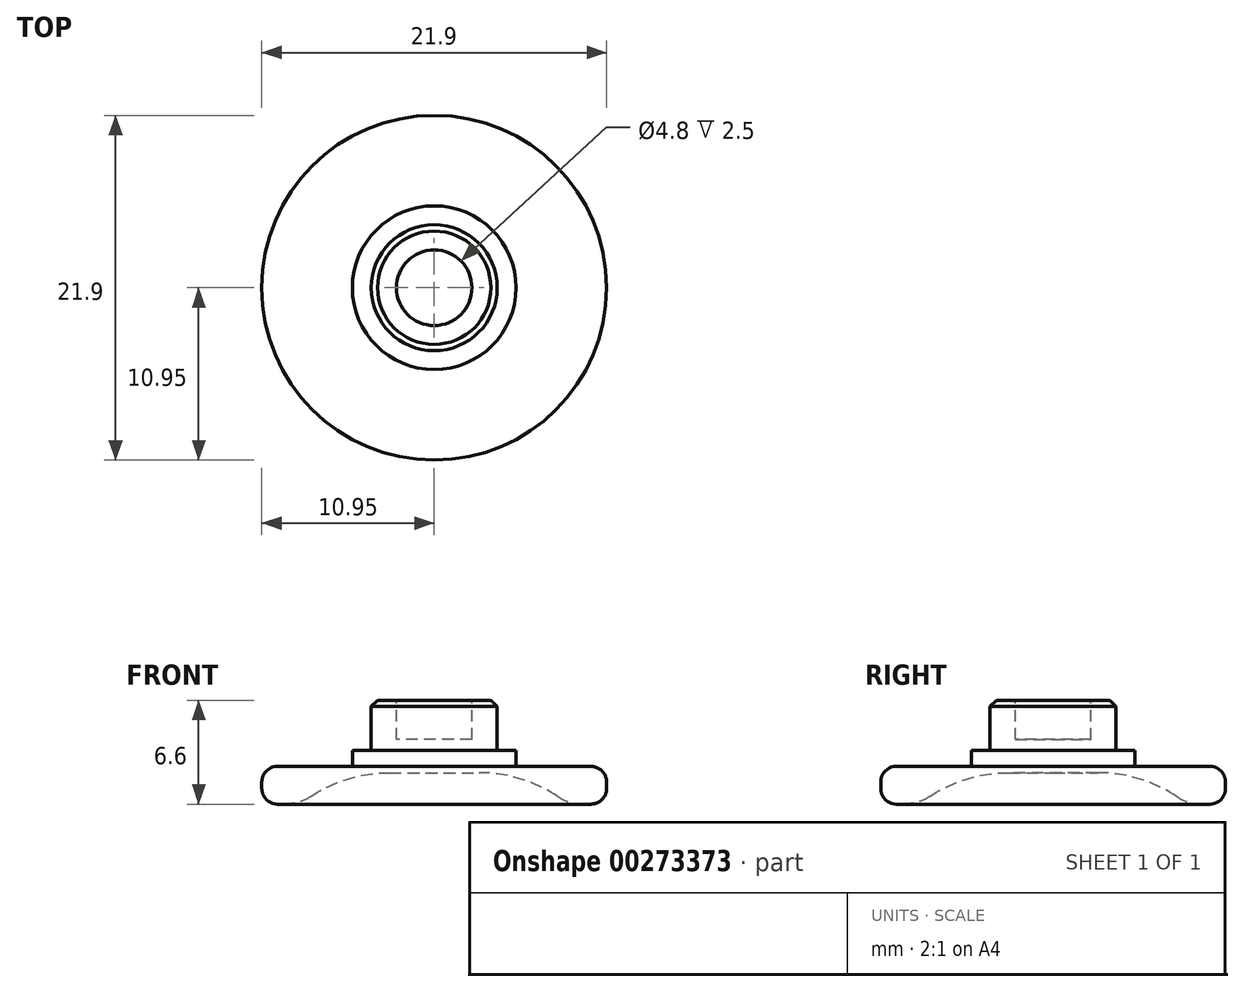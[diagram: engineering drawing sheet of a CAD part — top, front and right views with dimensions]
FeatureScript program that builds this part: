
annotation { "Feature Type Name" : "Feature", "Feature Type Description" : "" }
export const myFeature = defineFeature(function(context is Context, id is Id, definition is map)
    precondition{}
    {
        {
            var Q0;
            Q0=qCreatedBy(makeId("Top.planeOp"),FACE);
            var sketch = newSketch(context, id + "F0", { "sketchPlane" : qUnion([Q0])});
            skCircle(sketch, "E0", {"center": v(0, 0) * mm, "radius": 10.95 * mm});
            skSolve(sketch);
        }
        {
            var Q0;
            Q0=makeQuery(id+"F0.imprint","IMPRINT",FACE,{"disambiguationData":[TD([[makeQuery(id+"F0.imprint","IMPRINT",EDGE,{"derivedFrom":sQuery(id+"F0.wireOp",EDGE,"E0")}),1.0]])]});
            extrude(context, id + "F1", {"entities" : qUnion([Q0]), "depth" : 2.4 * mm});
        }
        {
            var Q0;
            Q0=makeQuery(id+"F1.opExtrude","CAP_FACE",FACE,{"disambiguationData":[OSD([sQuery(id+"F0.wireOp",EDGE,"E0")])],"isStart":false});
            var sketch = newSketch(context, id + "F2", { "sketchPlane" : qUnion([Q0])});
            skCircle(sketch, "E1", {"center": v(0, 0) * mm, "radius": 4 * mm});
            skSolve(sketch);
        }
        {
            var Q0;
            Q0=makeQuery(id+"F2.imprint","IMPRINT",FACE,{"disambiguationData":[TD([[makeQuery(id+"F2.imprint","IMPRINT",EDGE,{"derivedFrom":sQuery(id+"F2.wireOp",EDGE,"E1")}),1.0]])]});
            extrude(context, id + "F3", {"entities" : qUnion([Q0]), "operationType" : NewBodyOperationType.ADD, "depth" : 4.2 * mm});
        }
        {
            var Q0;
            Q0=makeQuery(id+"F1.opExtrude","CAP_EDGE",EDGE,{"disambiguationData":[OSD([sQuery(id+"F0.wireOp",EDGE,"E0")])],"isStart":false});
            fillet(context, id + "F4", {"entities" : qUnion([Q0]), "radius" : 1 * mm, "tangentPropagation" : true, "allowEdgeOverflow" : false});
        }
        {
            var Q0;
            Q0=makeQuery(id+"F1.opExtrude","CAP_FACE",FACE,{"disambiguationData":[OSD([sQuery(id+"F0.wireOp",EDGE,"E0")])],"isStart":false});
            var sketch = newSketch(context, id + "F5", { "sketchPlane" : qUnion([Q0])});
            skCircle(sketch, "E2", {"center": v(0, 0) * mm, "radius": 5.2 * mm});
            skSolve(sketch);
        }
        {
            var Q0;
            Q0=makeQuery(id+"F5.imprint","IMPRINT",FACE,{"disambiguationData":[TD([[makeQuery(id+"F5.imprint","IMPRINT",EDGE,{"derivedFrom":sQuery(id+"F5.wireOp",EDGE,"E2")}),1.0]])]});
            extrude(context, id + "F6", {"entities" : qUnion([Q0]), "operationType" : NewBodyOperationType.ADD, "depth" : 1 * mm});
        }
        {
            var Q0;
            Q0=makeQuery(id+"F1.opExtrude","CAP_EDGE",EDGE,{"disambiguationData":[OSD([sQuery(id+"F0.wireOp",EDGE,"E0")])],"isStart":true});
            fillet(context, id + "F7", {"entities" : qUnion([Q0]), "radius" : 1 * mm, "tangentPropagation" : true, "allowEdgeOverflow" : false});
        }
        {
            var Q0;
            Q0=makeQuery(id+"F1.opExtrude","CAP_FACE",FACE,{"disambiguationData":[OSD([sQuery(id+"F0.wireOp",EDGE,"E0")])],"isStart":true});
            var sketch = newSketch(context, id + "F8", { "sketchPlane" : qUnion([Q0])});
            skCircle(sketch, "E3", {"center": v(0, 0) * mm, "radius": 8.5 * mm});
            skSolve(sketch);
        }
        {
            var Q0;
            Q0=makeQuery(id+"F8.imprint","IMPRINT",FACE,{"disambiguationData":[TD([[makeQuery(id+"F8.imprint","IMPRINT",EDGE,{"derivedFrom":sQuery(id+"F8.wireOp",EDGE,"E3")}),1.0]])]});
            extrude(context, id + "F9", {"entities" : qUnion([Q0]), "operationType" : NewBodyOperationType.REMOVE, "oppositeDirection" : true, "depth" : 2 * mm});
        }
        {
            var Q0;
            Q0=makeQuery(id+"F9.boolean.opBoolean","COPY",EDGE,{"derivedFrom":makeQuery(id+"F9.opExtrude","CAP_EDGE",EDGE,{"disambiguationData":[OSD([sQuery(id+"F8.wireOp",EDGE,"E3")])],"isStart":false})});
            fillet(context, id + "F10", {"entities" : qUnion([Q0]), "radius" : 9 * mm, "tangentPropagation" : true, "allowEdgeOverflow" : false});
        }
        {
            var Q0;
            Q0=makeQuery(id+"F3.opExtrude","CAP_EDGE",EDGE,{"disambiguationData":[OSD([sQuery(id+"F2.wireOp",EDGE,"E1")])],"isStart":false});
            chamfer(context, id + "F11", {"entities" : qUnion([Q0]), "width" : .4 * mm, "tangentPropagation" : true});
        }
        {
            var Q0;
            Q0=makeQuery(id+"F10.opFillet","BLEND_EDGE",EDGE,{"blendedFrom":[makeQuery(id+"F9.boolean.opBoolean","COPY",EDGE,{"derivedFrom":makeQuery(id+"F9.opExtrude","CAP_EDGE",EDGE,{"disambiguationData":[OSD([sQuery(id+"F8.wireOp",EDGE,"E3")])],"isStart":false})}),makeQuery(id+"F1.opExtrude","CAP_FACE",FACE,{"disambiguationData":[OSD([sQuery(id+"F0.wireOp",EDGE,"E0")])],"isStart":true})],"blendedInto":[makeQuery(id+"F1.opExtrude","CAP_FACE",FACE,{"disambiguationData":[OSD([sQuery(id+"F0.wireOp",EDGE,"E0")])],"isStart":true})]});
            fillet(context, id + "F12", {"entities" : qUnion([Q0]), "radius" : 3 * mm, "tangentPropagation" : true, "allowEdgeOverflow" : false});
        }
        {
            var Q0;
            Q0=makeQuery(id+"F3.opExtrude","CAP_FACE",FACE,{"disambiguationData":[OSD([sQuery(id+"F2.wireOp",EDGE,"E1")])],"isStart":false});
            var sketch = newSketch(context, id + "F13", { "sketchPlane" : qUnion([Q0])});
            skCircle(sketch, "E4", {"center": v(0, 0) * mm, "radius": 2.4 * mm});
            skSolve(sketch);
        }
        {
            var Q0;
            Q0=makeQuery(id+"F13.imprint","IMPRINT",FACE,{"disambiguationData":[TD([[makeQuery(id+"F13.imprint","IMPRINT",EDGE,{"derivedFrom":sQuery(id+"F13.wireOp",EDGE,"E4")}),1.0]])]});
            extrude(context, id + "F14", {"entities" : qUnion([Q0]), "operationType" : NewBodyOperationType.REMOVE, "oppositeDirection" : true, "depth" : 2.5 * mm});
        }
    });
